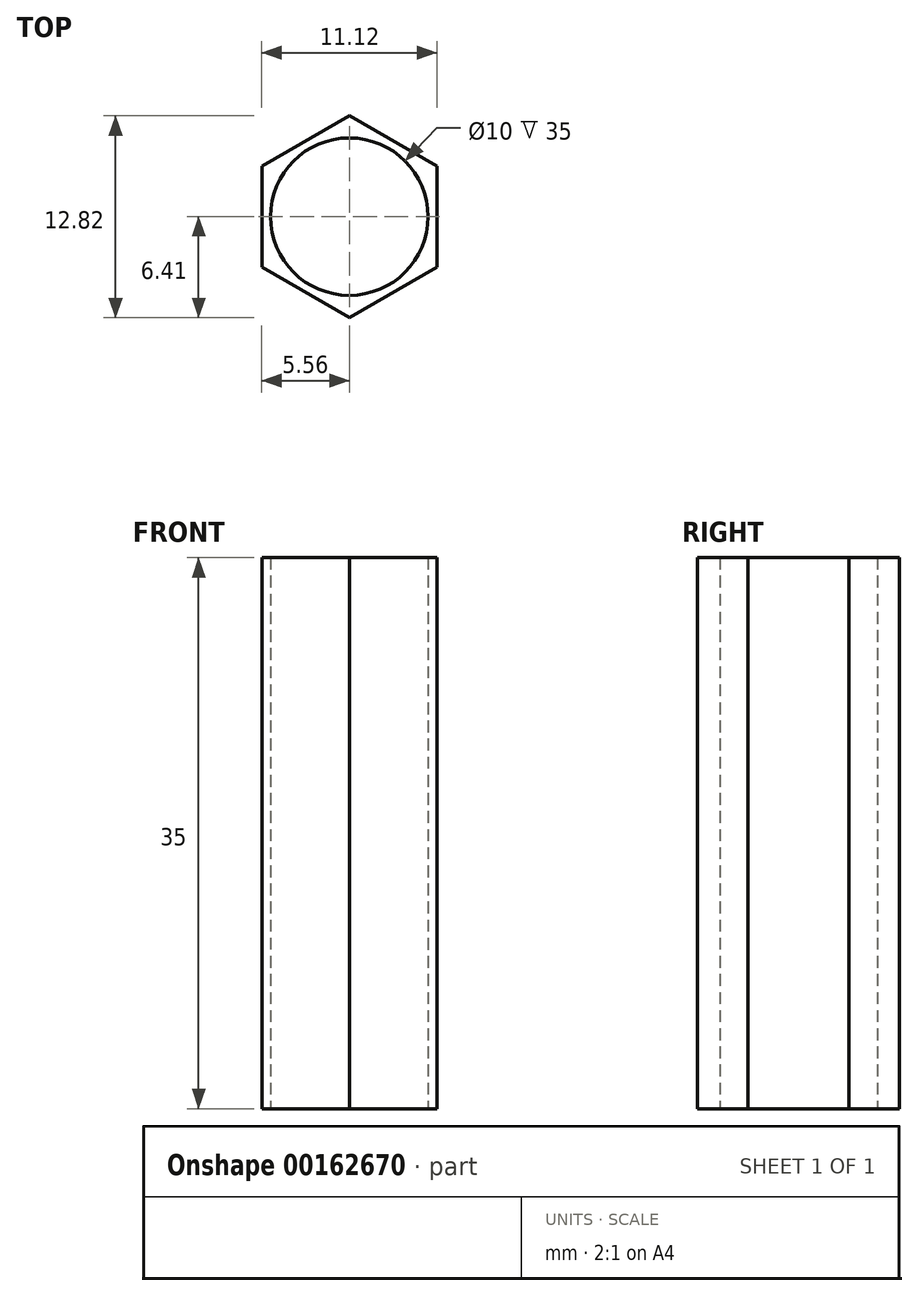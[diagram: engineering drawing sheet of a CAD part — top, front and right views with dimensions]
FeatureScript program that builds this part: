
annotation { "Feature Type Name" : "Feature", "Feature Type Description" : "" }
export const myFeature = defineFeature(function(context is Context, id is Id, definition is map)
    precondition{}
    {
        {
            var Q0;
            Q0=qCreatedBy(makeId("Top.planeOp"),FACE);
            var sketch = newSketch(context, id + "F0", { "sketchPlane" : qUnion([Q0])});
            skCircle(sketch, "E0.cCircle", {"center": v(0, 0) * mm, "radius": 5.56 * mm, "construction": true});
            skLineSegment(sketch, "E0.0", {"start": v(-5.56, -3.2) * mm, "end": v(-5.56, 3.2) * mm});
            skLineSegment(sketch, "E0.1", {"start": v(-5.56, 3.2) * mm, "end": v(0, 6.41) * mm});
            skLineSegment(sketch, "E0.2", {"start": v(0, 6.41) * mm, "end": v(5.55, 3.2) * mm});
            skLineSegment(sketch, "E0.3", {"start": v(5.55, 3.2) * mm, "end": v(5.56, -3.2) * mm});
            skLineSegment(sketch, "E0.4", {"start": v(5.56, -3.2) * mm, "end": v(0, -6.41) * mm});
            skLineSegment(sketch, "E0.5", {"start": v(0, -6.41) * mm, "end": v(-5.55, -3.2) * mm});
            skPoint(sketch, "E0.0.midPoint", {"position": v(-5.55, 0) * mm});
            skCircle(sketch, "E1", {"center": v(0, 0) * mm, "radius": 5 * mm});
            skSolve(sketch);
        }
        {
            var Q0;
            Q0 = qSketchRegion(id + "F0", true);
            extrude(context, id + "F1", {"entities" : qUnion([Q0]), "depth" : 35 * mm, "offsetDistance" : 25 * mm});
        }
    });
